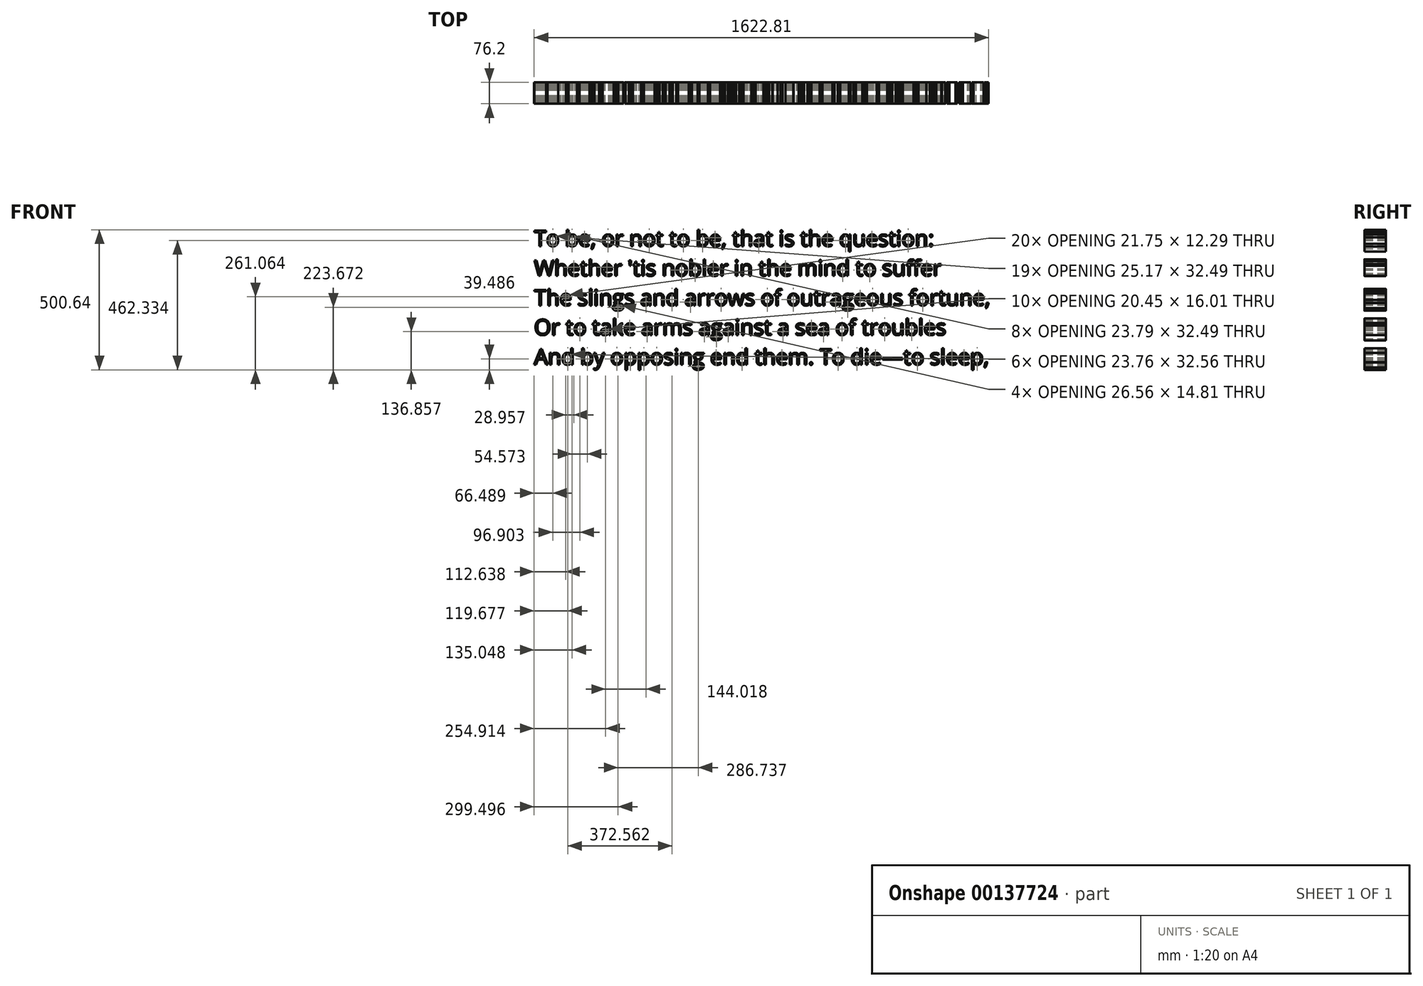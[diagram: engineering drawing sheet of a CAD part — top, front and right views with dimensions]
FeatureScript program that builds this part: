
annotation { "Feature Type Name" : "Feature", "Feature Type Description" : "" }
export const myFeature = defineFeature(function(context is Context, id is Id, definition is map)
    precondition{}
    {
        {
            var Q0;
            Q0=qCreatedBy(makeId("Front.planeOp"),FACE);
            var sketch = newSketch(context, id + "F0", { "sketchPlane" : qUnion([Q0])});
            skText(sketch, "E0", { "text": "To be, or not to be, that is the question:\nWhether \'tis nobler in the mind to suffer\nThe slings and arrows of outrageous fortune,\nOr to take arms against a sea of troubles\nAnd by opposing end them. To die—to sleep,\n", "fontName": "OpenSans-Regular.ttf"});
            const initialGuessF0  = {"E0": [-1.62791, 0, 1, 0, 0.05597]};
            skSetInitialGuess(sketch, initialGuessF0);
            skSolve(sketch);
        }
        {
            var Q0;
            Q0 = qSketchRegion(id + "F0", true);
            extrude(context, id + "F1", {"entities" : qUnion([Q0]), "oppositeDirection" : true, "depth" : 76.2 * mm});
        }
    });
